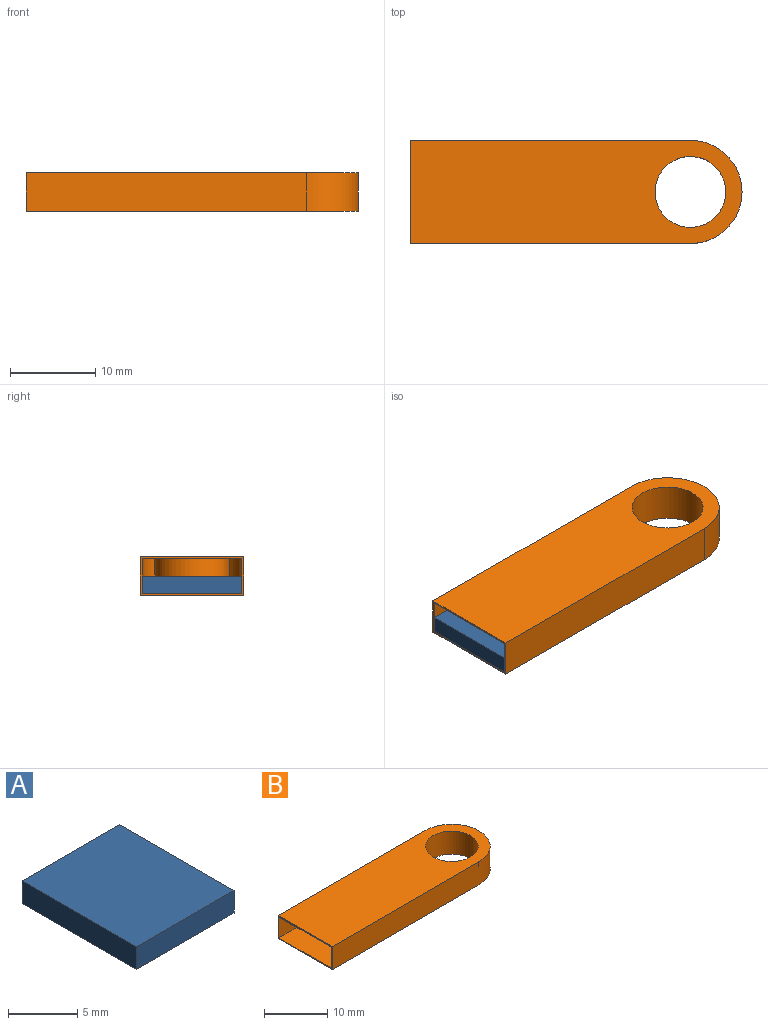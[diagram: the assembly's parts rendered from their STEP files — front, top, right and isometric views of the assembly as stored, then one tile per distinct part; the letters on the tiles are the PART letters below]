
ASSEMBLY  parts=2 mates=1
PART A: 6 faces, bbox 10x11.7x2 mm
  f0: plane 10x2mm, normal (0,1,0), area 20mm2, adj f1,f3,f4,f5
  f1: plane 11.7x2mm, normal (-1,0,0), area 23.4mm2, adj f0,f2,f4,f5
  f2: plane 10x2mm, normal (0,-1,0), area 20mm2, adj f1,f3,f4,f5
  f3: plane 11.7x2mm, normal (1,0,0), area 23.4mm2, adj f0,f2,f4,f5
  f4: plane 11.7x10mm, normal (0,0,1), area 117mm2, adj f0,f1,f2,f3
  f5: plane 11.7x10mm, normal (0,0,-1), area 117mm2, adj f0,f1,f2,f3
PART B: 13 faces, bbox 39x12.1x4.5 mm
  f0: plane 12.12x4.47mm, normal (-1,0,0), area 6.5mm2, adj f2,f4,f5,f6,f8,f10,f11,f12
  f1: cylinder r=6.06mm len=12.12mm, axis (0,0,-1), area 85.1mm2, adj f2,f4,f5,f6
  f2: plane 32.94x4.47mm, normal (0,1,0), area 147.2mm2, adj f0,f1,f5,f6
  f3: cylinder r=4.16mm len=8.32mm, axis (0,0,-1), area 116.8mm2, adj f5,f6
  f4: plane 32.94x4.47mm, normal (0,-1,0), area 147.2mm2, adj f0,f1,f5,f6
  f5: plane 39x12.12mm, normal (0,0,1), area 402.6mm2, adj f0,f1,f2,f3,f4
  f6: plane 39x12.12mm, normal (0,0,-1), area 402.6mm2, adj f0,f1,f2,f3,f4
  f7: cylinder r=5.86mm len=11.72mm, axis (0,0,-1), area 74.9mm2, adj f8,f10,f11,f12
  f8: plane 32.94x4.07mm, normal (0,-1,0), area 134.1mm2, adj f0,f7,f11,f12
  f9: cylinder r=4.36mm len=8.72mm, axis (0,0,-1), area 111.5mm2, adj f11,f12
  f10: plane 32.94x4.07mm, normal (0,1,0), area 134.1mm2, adj f0,f7,f11,f12
  f11: plane 38.8x11.72mm, normal (0,0,-1), area 380.3mm2, adj f0,f7,f8,f9,f10
  f12: plane 38.8x11.72mm, normal (0,0,1), area 380.3mm2, adj f0,f7,f8,f9,f10
PLACE A rot(axis=(1,0,0),180deg) t=(79.81,-22.77,6.89)mm
PLACE B t=(-2.78,-4.81,4.69)mm
MATE fastened A.f4 <-> B.f12  axis (0,0,-1) through (-35.72,-4.81,4.89)mm
